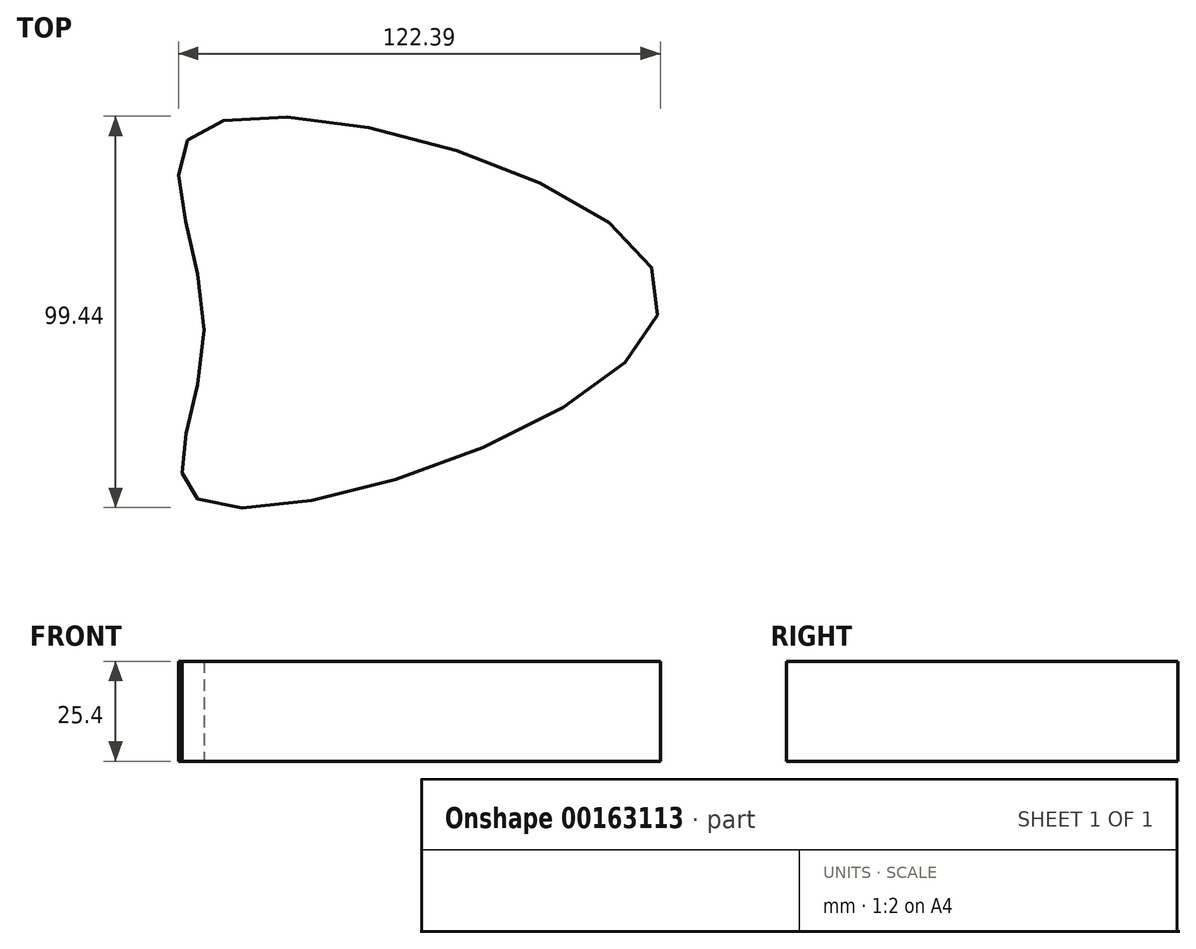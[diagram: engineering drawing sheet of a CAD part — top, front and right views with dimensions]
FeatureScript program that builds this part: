
annotation { "Feature Type Name" : "Feature", "Feature Type Description" : "" }
export const myFeature = defineFeature(function(context is Context, id is Id, definition is map)
    precondition{}
    {
        {
            var Q0;
            Q0=qCreatedBy(makeId("Top.planeOp"),FACE);
            var sketch = newSketch(context, id + "F0", { "sketchPlane" : qUnion([Q0])});
            skFitSpline(sketch, "E0", {"points": [v(-67.65, -6.47) * mm, v(-67.65, 45.12) * mm, v(48.26, 1.83) * mm, v(-67.65, -50.22) * mm, v(-67.65, -6.47) * mm]});
            skSolve(sketch);
        }
        {
            var Q0;
            Q0=makeQuery(id+"F0.imprint","IMPRINT",FACE,{"disambiguationData":[TD([[makeQuery(id+"F0.imprint","IMPRINT",EDGE,{"derivedFrom":sQuery(id+"F0.wireOp",EDGE,"E0")}),-1.0]])]});
            extrude(context, id + "F1", {"entities" : qUnion([Q0]), "depth" : 25.4 * mm});
        }
    });
